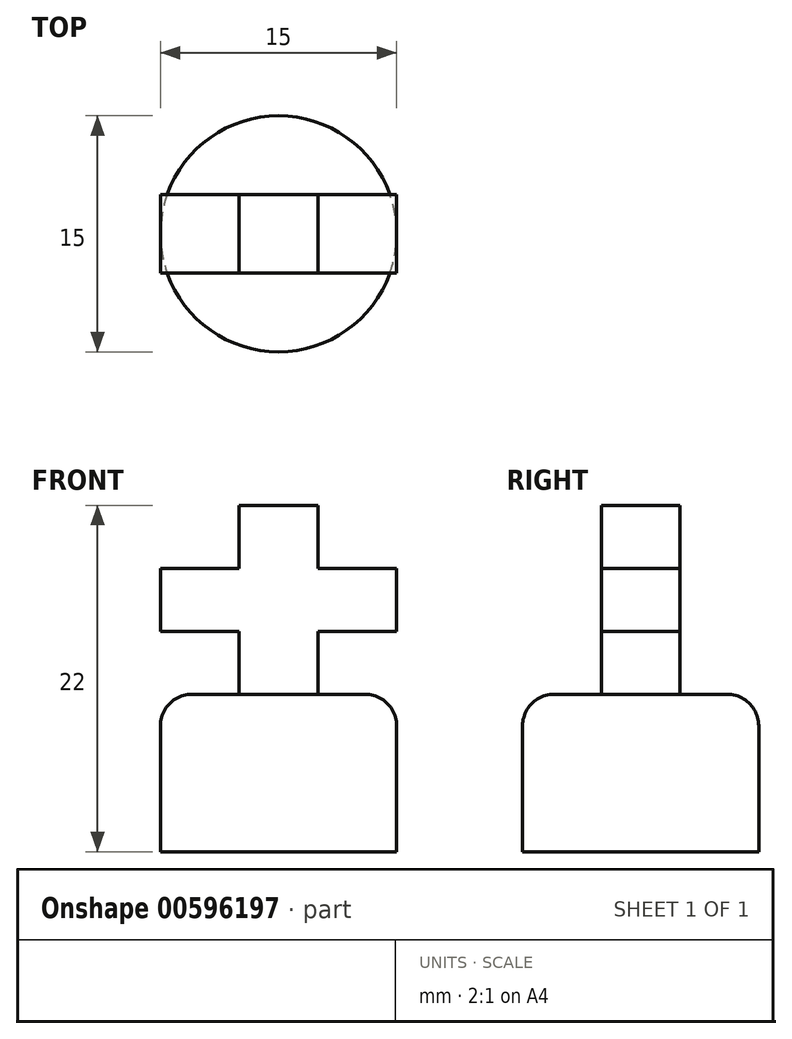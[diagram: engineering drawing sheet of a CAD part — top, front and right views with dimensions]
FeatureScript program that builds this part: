
annotation { "Feature Type Name" : "Feature", "Feature Type Description" : "" }
export const myFeature = defineFeature(function(context is Context, id is Id, definition is map)
    precondition{}
    {
        {
            var Q0;
            Q0=qCreatedBy(makeId("Top.planeOp"),FACE);
            var sketch = newSketch(context, id + "F0", { "sketchPlane" : qUnion([Q0])});
            skCircle(sketch, "E0", {"center": v(0, 0) * mm, "radius": 7.5 * mm});
            skSolve(sketch);
        }
        {
            var Q0;
            Q0 = qSketchRegion(id + "F0", true);
            extrude(context, id + "F1", {"entities" : qUnion([Q0]), "depth" : 10 * mm, "offsetDistance" : 25 * mm});
        }
        {
            var Q0;
            Q0=qCreatedBy(makeId("Front.planeOp"),FACE);
            var sketch = newSketch(context, id + "F2", { "sketchPlane" : qUnion([Q0])});
            skLineSegment(sketch, "E1.bottom", {"start": v(-2.5, 22) * mm, "end": v(2.5, 22) * mm});
            skLineSegment(sketch, "E1.top", {"start": v(-2.5, 10) * mm, "end": v(2.5, 10) * mm});
            skLineSegment(sketch, "E1.left", {"start": v(-2.5, 22) * mm, "end": v(-2.5, 18) * mm});
            skLineSegment(sketch, "E1.right", {"start": v(2.5, 22) * mm, "end": v(2.5, 18) * mm});
            skLineSegment(sketch, "E2.bottom", {"start": v(-7.5, 18) * mm, "end": v(-2.5, 18) * mm});
            skLineSegment(sketch, "E2.top", {"start": v(-7.5, 14) * mm, "end": v(-2.5, 14) * mm});
            skLineSegment(sketch, "E2.left", {"start": v(-7.5, 18) * mm, "end": v(-7.5, 14) * mm});
            skLineSegment(sketch, "E2.right", {"start": v(7.5, 18) * mm, "end": v(7.5, 14) * mm});
            skLineSegment(sketch, "E3.trimOffspring", {"start": v(-2.5, 14) * mm, "end": v(-2.5, 10) * mm});
            skLineSegment(sketch, "E4.trimOffspring", {"start": v(2.5, 18) * mm, "end": v(7.5, 18) * mm});
            skLineSegment(sketch, "E5.trimOffspring", {"start": v(2.5, 14) * mm, "end": v(7.5, 14) * mm});
            skLineSegment(sketch, "E6.trimOffspring", {"start": v(2.5, 14) * mm, "end": v(2.5, 10) * mm});
            skPoint(sketch, "E7", {"position": v(0, 22) * mm});
            skSolve(sketch);
        }
        {
            var Q0;
            Q0 = qSketchRegion(id + "F2", true);
            extrude(context, id + "F3", {"entities" : qUnion([Q0]), "operationType" : NewBodyOperationType.ADD, "endBound" : BoundingType.SYMMETRIC, "depth" : 5 * mm, "offsetDistance" : 25 * mm});
        }
        {
            var Q0;
            Q0=makeQuery(id+"F1.opExtrude","CAP_EDGE",EDGE,{"disambiguationData":[OSD([sQuery(id+"F0.wireOp",EDGE,"E0")])],"isStart":false});
            fillet(context, id + "F4", {"entities" : qUnion([Q0]), "radius" : 2 * mm, "tangentPropagation" : true, "allowEdgeOverflow" : false});
        }
    });
